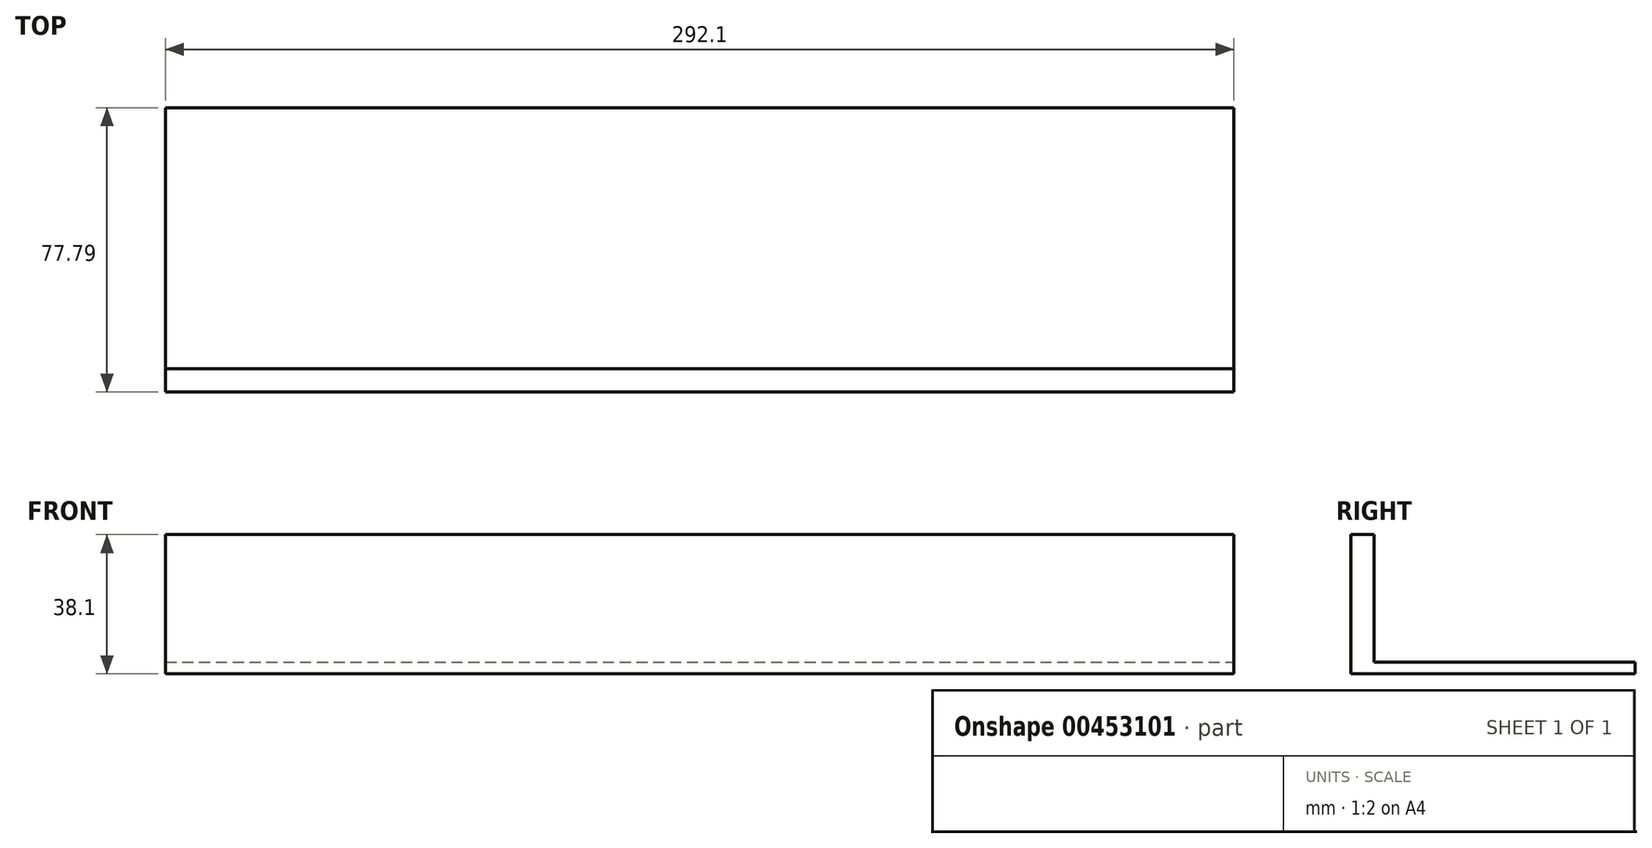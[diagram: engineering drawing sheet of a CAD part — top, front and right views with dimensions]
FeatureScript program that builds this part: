
annotation { "Feature Type Name" : "Feature", "Feature Type Description" : "" }
export const myFeature = defineFeature(function(context is Context, id is Id, definition is map)
    precondition{}
    {
        {
            var Q0;
            Q0=qCreatedBy(makeId("Top.planeOp"),FACE);
            var sketch = newSketch(context, id + "F0", { "sketchPlane" : qUnion([Q0])});
            skLineSegment(sketch, "E0.bottom", {"start": v(0, 0) * mm, "end": v(292.1, 0) * mm});
            skLineSegment(sketch, "E0.top", {"start": v(0, 71.44) * mm, "end": v(292.1, 71.44) * mm});
            skLineSegment(sketch, "E0.left", {"start": v(0, 0) * mm, "end": v(0, 71.44) * mm});
            skLineSegment(sketch, "E0.right", {"start": v(292.1, 0) * mm, "end": v(292.1, 71.44) * mm});
            skSolve(sketch);
        }
        {
            var Q0;
            Q0=makeQuery(id+"F0.imprint","IMPRINT",FACE,{"disambiguationData":[TD([[makeQuery(id+"F0.imprint","IMPRINT",EDGE,{"derivedFrom":sQuery(id+"F0.wireOp",EDGE,"E0.bottom")}),1.0]])]});
            extrude(context, id + "F1", {"entities" : qUnion([Q0]), "depth" : 3.17 * mm});
        }
        {
            var Q0;
            Q0=makeQuery(id+"F1.opExtrude","CAP_FACE",FACE,{"disambiguationData":[OSD([sQuery(id+"F0.wireOp",EDGE,"E0.bottom"),sQuery(id+"F0.wireOp",EDGE,"E0.top"),sQuery(id+"F0.wireOp",EDGE,"E0.left"),sQuery(id+"F0.wireOp",EDGE,"E0.right")])],"isStart":true});
            var sketch = newSketch(context, id + "F2", { "sketchPlane" : qUnion([Q0])});
            skLineSegment(sketch, "E1", {"start": v(0, 0) * mm, "end": v(0, -38.1) * mm});
            skLineSegment(sketch, "E2.bottom", {"start": v(0, -38.1) * mm, "end": v(292.1, -38.1) * mm});
            skLineSegment(sketch, "E2.top", {"start": v(0, 0) * mm, "end": v(292.1, 0) * mm});
            skLineSegment(sketch, "E2.left", {"start": v(0, -38.1) * mm, "end": v(0, 0) * mm});
            skLineSegment(sketch, "E2.right", {"start": v(292.1, -38.1) * mm, "end": v(292.1, 0) * mm});
            skLineSegment(sketch, "E3.top", {"start": v(0, 6.35) * mm, "end": v(292.1, 6.35) * mm});
            skLineSegment(sketch, "E3.left", {"start": v(0, 0) * mm, "end": v(0, 6.35) * mm});
            skLineSegment(sketch, "E3.right", {"start": v(292.1, 0) * mm, "end": v(292.1, 6.35) * mm});
            skSolve(sketch);
        }
        {
            var Q0;
            Q0=makeQuery(id+"F2.imprint","IMPRINT",FACE,{"disambiguationData":[TD([[makeQuery(id+"F2.imprint","IMPRINT",EDGE,{"derivedFrom":sQuery(id+"F2.wireOp",EDGE,"E2.top")}),1.0]])]});
            extrude(context, id + "F3", {"entities" : qUnion([Q0]), "operationType" : NewBodyOperationType.ADD, "oppositeDirection" : true, "depth" : 38.1 * mm});
        }
    });
